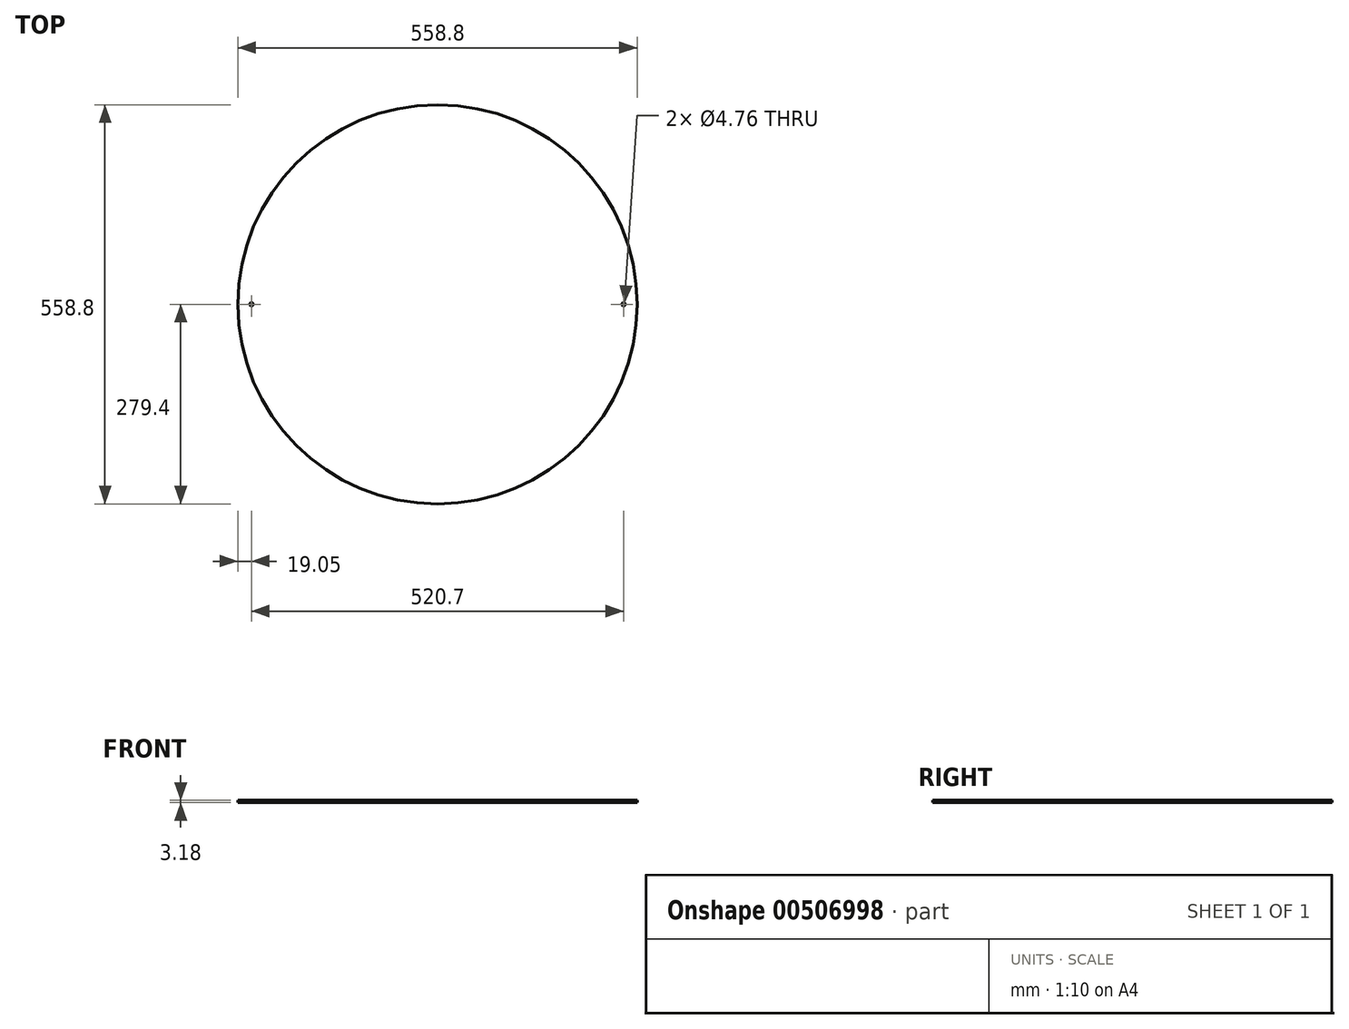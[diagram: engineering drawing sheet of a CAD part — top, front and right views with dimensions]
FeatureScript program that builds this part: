
annotation { "Feature Type Name" : "Feature", "Feature Type Description" : "" }
export const myFeature = defineFeature(function(context is Context, id is Id, definition is map)
    precondition{}
    {
        {
            var Q0;
            Q0=qCreatedBy(makeId("Top.planeOp"),FACE);
            var sketch = newSketch(context, id + "F0", { "sketchPlane" : qUnion([Q0])});
            skCircle(sketch, "E0", {"center": v(0, 0) * mm, "radius": 279.4 * mm});
            skCircle(sketch, "E1", {"center": v(0, 0) * mm, "radius": 241.3 * mm});
            skCircle(sketch, "E2", {"center": v(0, 0) * mm, "radius": 260.35 * mm, "construction": true});
            skLineSegment(sketch, "E3", {"start": v(-307.44, 0) * mm, "end": v(302.85, 0) * mm, "construction": true});
            skCircle(sketch, "E4", {"center": v(-260.35, 0) * mm, "radius": 2.38 * mm});
            skCircle(sketch, "E5.MirrorC", {"center": v(260.35, 0) * mm, "radius": 2.38 * mm});
            skSolve(sketch);
        }
        {
            var Q0;
            Q0 = qSketchRegion(id + "F0", true);
            var Q1;
            Q1=makeQuery(id+"F0.imprint","IMPRINT",FACE,{"disambiguationData":[TD([[makeQuery(id+"F0.imprint","IMPRINT",EDGE,{"derivedFrom":sQuery(id+"F0.wireOp",EDGE,"E1")}),1.0]])]});
            extrude(context, id + "F1", {"entities" : qUnion([Q0, Q1]), "depth" : 3.17 * mm});
        }
    });
